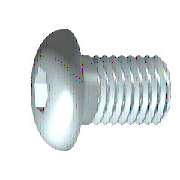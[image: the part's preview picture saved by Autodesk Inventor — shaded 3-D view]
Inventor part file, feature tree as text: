
AUTODESK INVENTOR PART (.ipt)
format: ipt  version: 2013 (Build 170138000, 138)  size: 190,464 bytes
history: native  units: mm (DEFAULTED — no unit token found)
features: sketch x2, extrude x1, plane x1, fillet x1
ambient origin geometry x7: Origin, YZ Plane, XY Plane, X Axis, Y Axis, Z Axis, Center Point
bodies: Solid1 (feature_tree), Body (feature_tree)
feature tree (5):
  extrude  "Slot"  Depth=1.59014mm
  plane  "Work Plane1"
  fillet  "Fillet2"  Radius=1.8542mm
  sketch  "Sketch1"  dims[d1=11.10976mm d2=1.59014mm d3=1.8542mm]
  sketch  "Sketch2"  dims[d4=1.1176mm d5=60.0deg d6=3.5052mm d7=3.5052mm d8=2.287693mm d9=6.6548mm d10=90.0deg d11=10.0mm d12=0.0mm d13=11.10976mm d14=0.0mm d15=0.486918mm d16=0.486918mm d17=1.6002mm d19=0.0mm d26=12.7mm d27=45.0deg d28=0.0mm d29=0.0mm d30=0.1mm]
